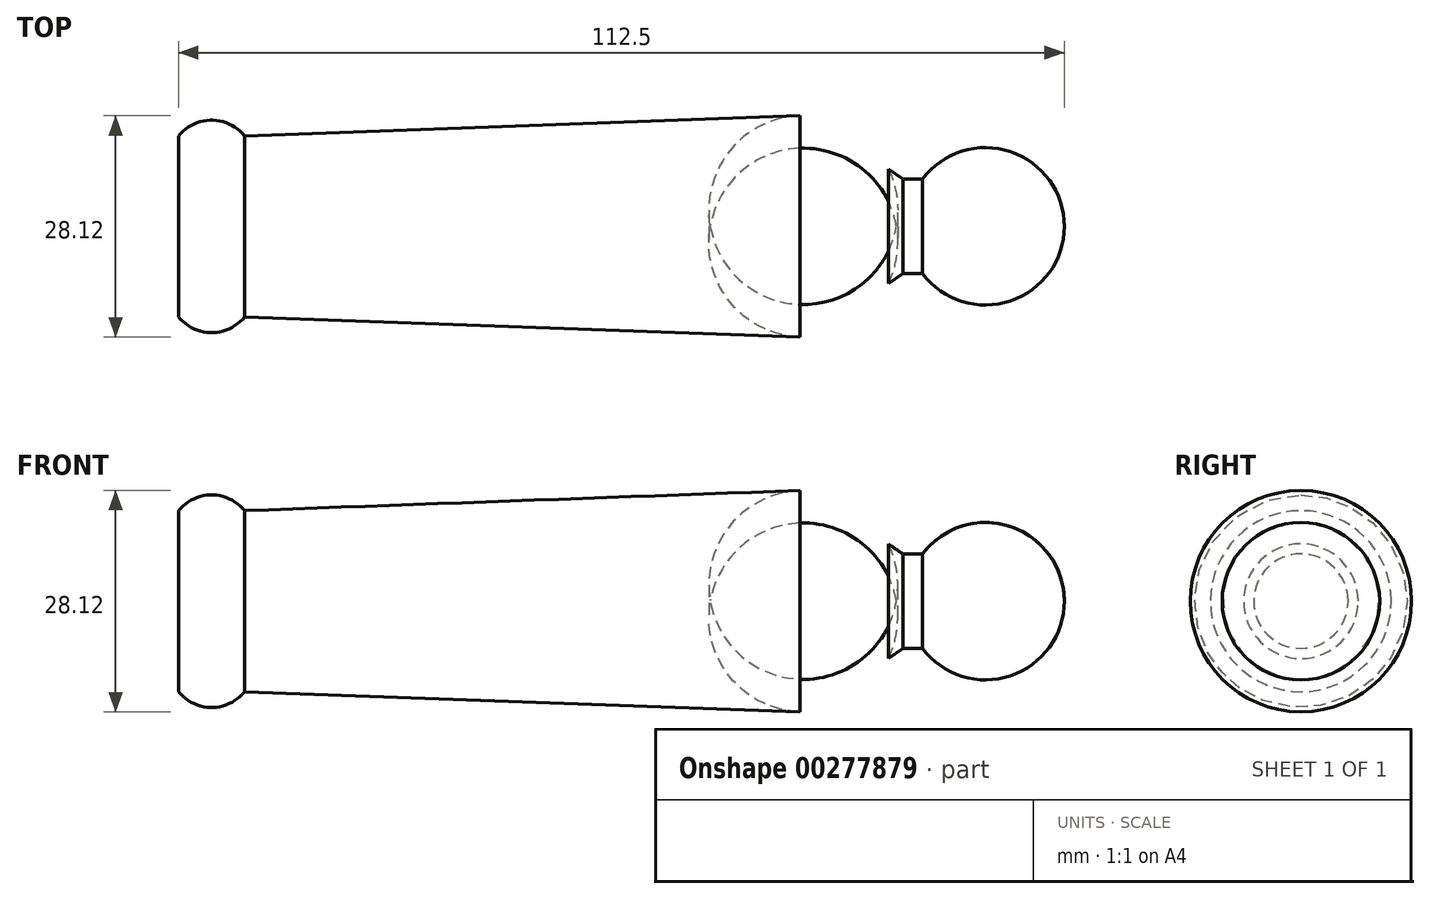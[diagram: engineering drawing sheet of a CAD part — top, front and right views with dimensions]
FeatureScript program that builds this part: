
annotation { "Feature Type Name" : "Feature", "Feature Type Description" : "" }
export const myFeature = defineFeature(function(context is Context, id is Id, definition is map)
    precondition{}
    {
        {
            var Q0;
            Q0=qCreatedBy(makeId("Front.planeOp"),FACE);
            var sketch = newSketch(context, id + "F0", { "sketchPlane" : qUnion([Q0])});
            skLineSegment(sketch, "E0.bottom", {"start": v(-40.18, 0) * mm, "end": v(43.82, 0) * mm});
            skLineSegment(sketch, "E0.top", {"start": v(-39.81, 11.5) * mm, "end": v(30.73, 14.06) * mm});
            skLineSegment(sketch, "E1.bottom", {"start": v(-40.18, 0) * mm, "end": v(-48.18, 0) * mm});
            skLineSegment(sketch, "E2.bottom", {"start": v(43.82, 0) * mm, "end": v(64.32, 0) * mm});
            skLineSegment(sketch, "E2.right", {"start": v(64.32, 0) * mm, "end": v(64.32, 0) * mm});
            skLineSegment(sketch, "E3.bottom", {"start": v(43.82, 0) * mm, "end": v(46.32, 0) * mm});
            skLineSegment(sketch, "E3.top", {"start": v(43.82, 6) * mm, "end": v(46.32, 6) * mm});
            skLineSegment(sketch, "E3.left", {"start": v(43.82, 0) * mm, "end": v(43.82, 6) * mm, "construction": true});
            skLineSegment(sketch, "E3.right", {"start": v(46.32, 0) * mm, "end": v(46.32, 6) * mm, "construction": true});
            skArc(sketch, "E4", {"start": v(64.32, 0) * mm, "mid": v(57.48, 9.49) * mm, "end": v(46.32, 6) * mm});
            skPoint(sketch, "E5", {"position": v(29.08, 14) * mm});
            skLineSegment(sketch, "E6", {"start": v(-48.18, 11.5) * mm, "end": v(-48.18, 0) * mm});
            skArc(sketch, "E7.filletArc", {"start": v(41.98, 7.28) * mm, "mid": v(37.37, 12.34) * mm, "end": v(30.73, 14.06) * mm});
            skArc(sketch, "E8", {"start": v(-39.81, 11.5) * mm, "mid": v(-44, 13.5) * mm, "end": v(-48.18, 11.5) * mm});
            skPoint(sketch, "E9", {"position": v(-44, 13.5) * mm});
            skLineSegment(sketch, "E10", {"start": v(43.82, 6) * mm, "end": v(41.98, 7.28) * mm});
            skLineSegment(sketch, "E11.0", {"start": v(-49.18, 11.83) * mm, "end": v(-49.18, 0) * mm});
            skArc(sketch, "E11.1", {"start": v(65.32, 0) * mm, "mid": v(58.04, 10.35) * mm, "end": v(45.84, 7) * mm});
            skLineSegment(sketch, "E11.3", {"start": v(-39.37, 12.51) * mm, "end": v(30.7, 15.06) * mm});
            skArc(sketch, "E11.4", {"start": v(-39.37, 12.51) * mm, "mid": v(-44.44, 14.48) * mm, "end": v(-49.18, 11.83) * mm});
            skLineSegment(sketch, "E12.0", {"start": v(44.13, 7) * mm, "end": v(45.84, 7) * mm});
            skLineSegment(sketch, "E12.1", {"start": v(44.13, 7) * mm, "end": v(42.76, 7.95) * mm});
            skArc(sketch, "E13.trimOffspring", {"start": v(42.76, 7.95) * mm, "mid": v(37.77, 13.27) * mm, "end": v(30.7, 15.06) * mm});
            skSolve(sketch);
        }
        {
            var Q0;
            Q0 = qSketchRegion(id + "F0", true);
            var Q1;
            Q1=sQuery(id+"F0.wireOp",EDGE,"E0.bottom");
            revolve(context, id + "F1", {"entities" : qUnion([Q0]), "axis" : qUnion([Q1]), "revolveType" : RevolveType.FULL});
        }
    });
